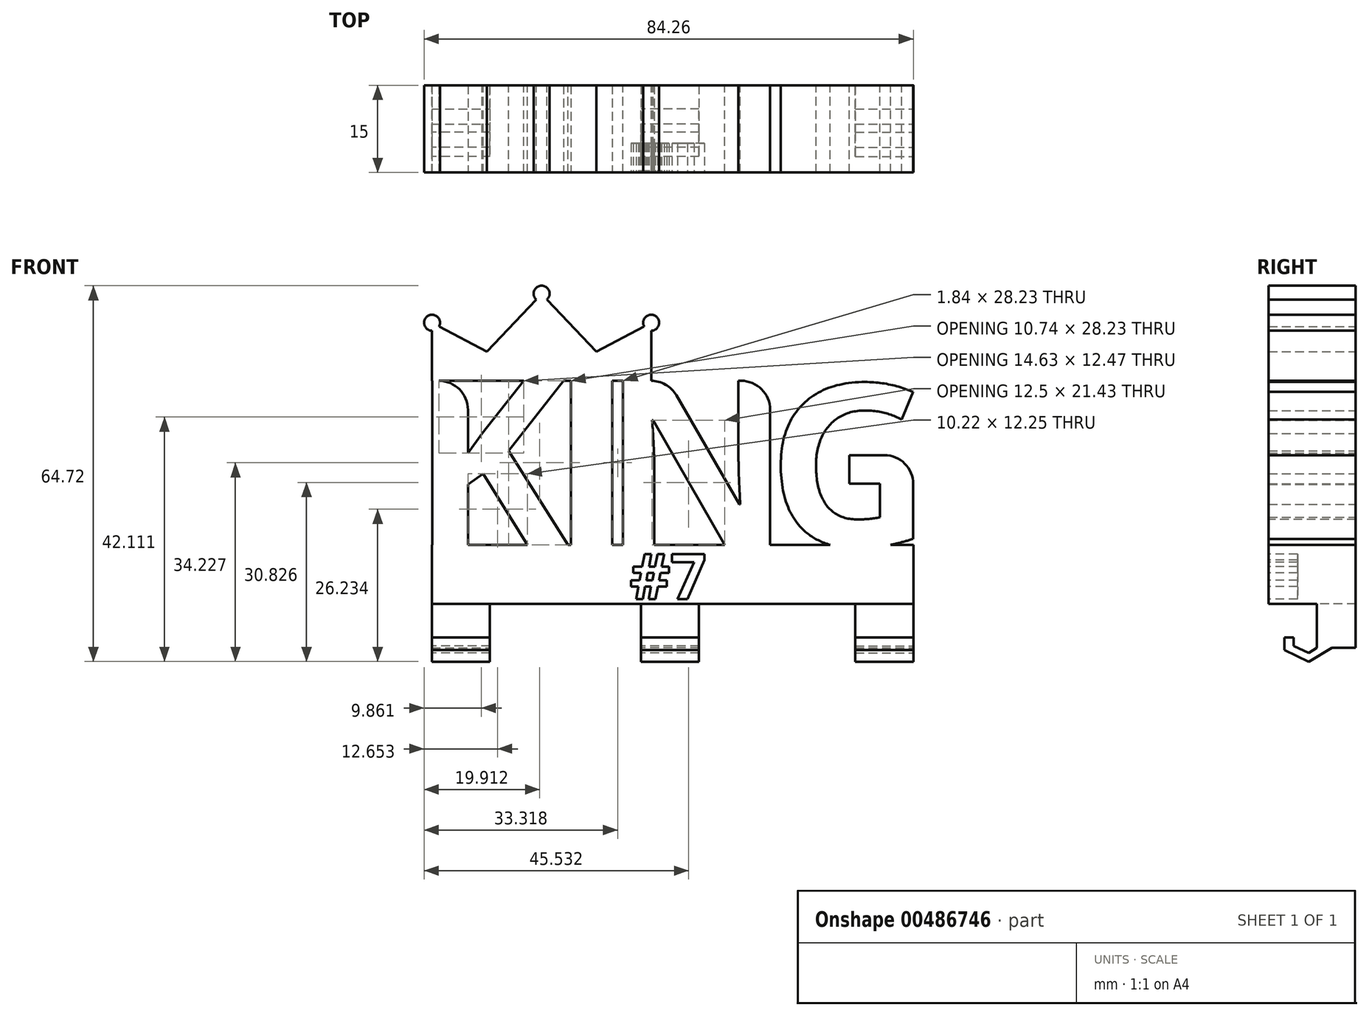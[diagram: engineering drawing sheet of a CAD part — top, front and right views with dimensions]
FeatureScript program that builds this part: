
annotation { "Feature Type Name" : "Feature", "Feature Type Description" : "" }
export const myFeature = defineFeature(function(context is Context, id is Id, definition is map)
    precondition{}
    {
        {
            var Q0;
            Q0=qCreatedBy(makeId("Front.planeOp"),FACE);
            var sketch = newSketch(context, id + "F0", { "sketchPlane" : qUnion([Q0])});
            skLineSegment(sketch, "E0.bottom", {"start": v(-40.14, -20.06) * mm, "end": v(40.04, -20.06) * mm});
            skLineSegment(sketch, "E0.top", {"start": v(-40.14, -9.99) * mm, "end": v(40.04, -9.99) * mm});
            skLineSegment(sketch, "E0.left", {"start": v(-40.14, -20.06) * mm, "end": v(-40.14, -9.99) * mm});
            skLineSegment(sketch, "E0.right", {"start": v(40.04, -20.06) * mm, "end": v(40.04, -9.99) * mm});
            skSolve(sketch);
        }
        {
            var Q0;
            Q0=makeQuery(id+"F0.imprint","IMPRINT",FACE,{"disambiguationData":[TD([[makeQuery(id+"F0.imprint","IMPRINT",EDGE,{"derivedFrom":sQuery(id+"F0.wireOp",EDGE,"E0.bottom")}),1.0]])]});
            extrude(context, id + "F1", {"entities" : qUnion([Q0]), "depth" : 15 * mm});
        }
        {
            var Q0;
            Q0=qCreatedBy(makeId("Front.planeOp"),FACE);
            var sketch = newSketch(context, id + "F2", { "sketchPlane" : qUnion([Q0])});
            skText(sketch, "E1", { "text": "K", "fontName": "OpenSans-Bold.ttf"});
            const initialGuessF2  = {"E1": [-0.0434, -0.00988, 1, 0, 0.02932]};
            skSetInitialGuess(sketch, initialGuessF2);
            skSolve(sketch);
        }
        {
            var Q0;
            Q0 = qSketchRegion(id + "F2", true);
            extrude(context, id + "F3", {"entities" : qUnion([Q0]), "depth" : 15 * mm});
        }
        {
            var Q0;
            Q0=qCreatedBy(makeId("Front.planeOp"),FACE);
            var sketch = newSketch(context, id + "F4", { "sketchPlane" : qUnion([Q0])});
            skLineSegment(sketch, "E2.bottom", {"start": v(-15.84, 19.23) * mm, "end": v(-8.72, 19.23) * mm});
            skLineSegment(sketch, "E2.top", {"start": v(-15.84, -9.97) * mm, "end": v(-8.72, -9.97) * mm});
            skLineSegment(sketch, "E2.left", {"start": v(-15.84, 19.23) * mm, "end": v(-15.84, -9.97) * mm});
            skLineSegment(sketch, "E2.right", {"start": v(-8.72, 19.23) * mm, "end": v(-8.72, -9.97) * mm});
            skSolve(sketch);
        }
        {
            var Q0;
            Q0 = qSketchRegion(id + "F4", true);
            extrude(context, id + "F5", {"entities" : qUnion([Q0]), "depth" : 15 * mm});
        }
        {
            var Q0;
            Q0=qCreatedBy(makeId("Front.planeOp"),FACE);
            var sketch = newSketch(context, id + "F6", { "sketchPlane" : qUnion([Q0])});
            skText(sketch, "E3", { "text": "N", "fontName": "OpenSans-Bold.ttf"});
            const initialGuessF6  = {"E3": [-0.01048, -0.01007, 1, 0, 0.02883]};
            skSetInitialGuess(sketch, initialGuessF6);
            skSolve(sketch);
        }
        {
            var Q0;
            Q0 = qSketchRegion(id + "F6", true);
            extrude(context, id + "F7", {"entities" : qUnion([Q0]), "operationType" : NewBodyOperationType.ADD, "depth" : 15 * mm});
        }
        {
            var Q0;
            Q0=qCreatedBy(makeId("Front.planeOp"),FACE);
            var sketch = newSketch(context, id + "F8", { "sketchPlane" : qUnion([Q0])});
            skText(sketch, "E4", { "text": "G", "fontName": "OpenSans-Bold.ttf"});
            const initialGuessF8  = {"E4": [0.01804, -0.01005, 1, 0, 0.02804]};
            skSetInitialGuess(sketch, initialGuessF8);
            skSolve(sketch);
        }
        {
            var Q0;
            Q0 = qSketchRegion(id + "F8", true);
            extrude(context, id + "F9", {"entities" : qUnion([Q0]), "operationType" : NewBodyOperationType.ADD, "depth" : 15 * mm});
        }
        {
            var Q0;
            Q0=qCreatedBy(makeId("Front.planeOp"),FACE);
            var sketch = newSketch(context, id + "F10", { "sketchPlane" : qUnion([Q0])});
            skLineSegment(sketch, "E5.bottom", {"start": v(-40.2, -19.96) * mm, "end": v(43.48, -19.96) * mm});
            skLineSegment(sketch, "E5.top", {"start": v(-40.2, -10) * mm, "end": v(43.48, -10) * mm});
            skLineSegment(sketch, "E5.left", {"start": v(-40.2, -19.96) * mm, "end": v(-40.2, -10) * mm});
            skLineSegment(sketch, "E5.right", {"start": v(43.48, -19.96) * mm, "end": v(43.48, -10) * mm});
            skSolve(sketch);
        }
        {
            var Q0;
            Q0 = qSketchRegion(id + "F10", true);
            extrude(context, id + "F11", {"entities" : qUnion([Q0]), "operationType" : NewBodyOperationType.ADD, "depth" : 15 * mm});
        }
        {
            var Q0;
            Q0=qCreatedBy(makeId("Front.planeOp"),FACE);
            var sketch = newSketch(context, id + "F12", { "sketchPlane" : qUnion([Q0])});
            skLineSegment(sketch, "E6.bottom", {"start": v(-46.89, 43.54) * mm, "end": v(51.78, 43.54) * mm});
            skLineSegment(sketch, "E6.top", {"start": v(-46.89, 18.35) * mm, "end": v(51.78, 18.35) * mm});
            skLineSegment(sketch, "E6.left", {"start": v(-46.89, 43.54) * mm, "end": v(-46.89, 18.35) * mm});
            skLineSegment(sketch, "E6.right", {"start": v(51.78, 43.54) * mm, "end": v(51.78, 18.35) * mm});
            skSolve(sketch);
        }
        {
            var Q0;
            Q0=makeQuery(id+"F12.imprint","IMPRINT",FACE,{"disambiguationData":[TD([[makeQuery(id+"F12.imprint","IMPRINT",EDGE,{"derivedFrom":sQuery(id+"F12.wireOp",EDGE,"E6.bottom")}),-1.0]])]});
            extrude(context, id + "F13", {"entities" : qUnion([Q0]), "operationType" : NewBodyOperationType.REMOVE, "depth" : 52.6 * mm});
        }
        {
            var Q0;
            Q0=qCreatedBy(makeId("Front.planeOp"),FACE);
            var sketch = newSketch(context, id + "F14", { "sketchPlane" : qUnion([Q0])});
            skLineSegment(sketch, "E7.bottom", {"start": v(-46.08, -4.47) * mm, "end": v(-39.9, -4.47) * mm});
            skLineSegment(sketch, "E7.top", {"start": v(-46.08, -23.6) * mm, "end": v(-39.9, -23.6) * mm});
            skLineSegment(sketch, "E7.left", {"start": v(-46.08, -4.47) * mm, "end": v(-46.08, -23.6) * mm});
            skLineSegment(sketch, "E7.right", {"start": v(-39.9, -4.47) * mm, "end": v(-39.9, -23.6) * mm});
            skSolve(sketch);
        }
        {
            var Q0;
            Q0=makeQuery(id+"F14.imprint","IMPRINT",FACE,{"disambiguationData":[TD([[makeQuery(id+"F14.imprint","IMPRINT",EDGE,{"derivedFrom":sQuery(id+"F14.wireOp",EDGE,"E7.bottom")}),-1.0]])]});
            extrude(context, id + "F15", {"entities" : qUnion([Q0]), "operationType" : NewBodyOperationType.REMOVE, "depth" : 25 * mm});
        }
        {
            var Q0;
            Q0=qCreatedBy(makeId("Front.planeOp"),FACE);
            var sketch = newSketch(context, id + "F16", { "sketchPlane" : qUnion([Q0])});
            skLineSegment(sketch, "E8.bottom", {"start": v(43.14, 5.6) * mm, "end": v(49.6, 5.6) * mm});
            skLineSegment(sketch, "E8.top", {"start": v(43.14, -21.5) * mm, "end": v(49.6, -21.5) * mm});
            skLineSegment(sketch, "E8.left", {"start": v(43.14, 5.6) * mm, "end": v(43.14, -21.5) * mm});
            skLineSegment(sketch, "E8.right", {"start": v(49.6, 5.6) * mm, "end": v(49.6, -21.5) * mm});
            skSolve(sketch);
        }
        {
            var Q0;
            Q0 = qSketchRegion(id + "F16", true);
            extrude(context, id + "F17", {"entities" : qUnion([Q0]), "operationType" : NewBodyOperationType.REMOVE, "depth" : 25 * mm});
        }
        {
            var Q0;
            Q0=qCreatedBy(makeId("Front.planeOp"),FACE);
            var sketch = newSketch(context, id + "F18", { "sketchPlane" : qUnion([Q0])});
            skLineSegment(sketch, "E9.bottom", {"start": v(-39.9, -18.54) * mm, "end": v(43.14, -18.54) * mm});
            skLineSegment(sketch, "E9.top", {"start": v(-39.9, -20.07) * mm, "end": v(43.14, -20.07) * mm});
            skLineSegment(sketch, "E9.left", {"start": v(-39.9, -18.54) * mm, "end": v(-39.9, -20.07) * mm});
            skLineSegment(sketch, "E9.right", {"start": v(43.14, -18.54) * mm, "end": v(43.14, -20.07) * mm});
            skSolve(sketch);
        }
        {
            var Q0;
            Q0 = qSketchRegion(id + "F18", true);
            extrude(context, id + "F19", {"entities" : qUnion([Q0]), "depth" : 15 * mm});
        }
        {
            var Q0;
            Q0=qCreatedBy(makeId("Front.planeOp"),FACE);
            var sketch = newSketch(context, id + "F20", { "sketchPlane" : qUnion([Q0])});
            skLineSegment(sketch, "E10.bottom", {"start": v(-39.9, -10.02) * mm, "end": v(43.14, -10.02) * mm});
            skLineSegment(sketch, "E10.top", {"start": v(-39.9, -9.88) * mm, "end": v(43.14, -9.88) * mm});
            skLineSegment(sketch, "E10.left", {"start": v(-39.9, -10.02) * mm, "end": v(-39.9, -9.88) * mm});
            skLineSegment(sketch, "E10.right", {"start": v(43.14, -10.02) * mm, "end": v(43.14, -9.88) * mm});
            skSolve(sketch);
        }
        {
            var Q0;
            Q0 = qSketchRegion(id + "F20", true);
            extrude(context, id + "F21", {"entities" : qUnion([Q0]), "operationType" : NewBodyOperationType.ADD, "depth" : 15 * mm});
        }
        {
            var Q0;
            Q0=qCreatedBy(makeId("Front.planeOp"),FACE);
            var sketch = newSketch(context, id + "F22", { "sketchPlane" : qUnion([Q0])});
            skLineSegment(sketch, "E11.bottom", {"start": v(-43.65, -8.35) * mm, "end": v(-39.8, -8.35) * mm});
            skLineSegment(sketch, "E11.top", {"start": v(-43.65, -21.4) * mm, "end": v(-39.8, -21.4) * mm});
            skLineSegment(sketch, "E11.left", {"start": v(-43.65, -8.35) * mm, "end": v(-43.65, -21.4) * mm});
            skLineSegment(sketch, "E11.right", {"start": v(-39.8, -8.35) * mm, "end": v(-39.8, -21.4) * mm});
            skSolve(sketch);
        }
        {
            var Q0;
            Q0 = qSketchRegion(id + "F22", true);
            extrude(context, id + "F23", {"entities" : qUnion([Q0]), "operationType" : NewBodyOperationType.REMOVE, "depth" : 25 * mm});
        }
        {
            var Q0;
            {var subQ54=sQuery(id+"F0.wireOp",EDGE,"E0.bottom");Q0=makeQuery(id+"F23.boolean.opBoolean","COPY",FACE,{"disambiguationData":[TD([makeQuery(id+"F1.opExtrude","SWEPT_FACE",FACE,{"disambiguationData":[OSD([subQ54])]})])],"derivedFrom":makeQuery(id+"F23.opExtrude","SWEPT_FACE",FACE,{"disambiguationData":[OSD([sQuery(id+"F22.wireOp",EDGE,"E11.right")])]})});}
            var sketch = newSketch(context, id + "F24", { "sketchPlane" : qUnion([Q0])});
            skLineSegment(sketch, "E12", {"start": v(4.05, -20.06) * mm, "end": v(4.05, -27.64) * mm});
            skLineSegment(sketch, "E13", {"start": v(4.05, -27.64) * mm, "end": v(8.1, -30) * mm});
            skLineSegment(sketch, "E14", {"start": v(8.1, -30) * mm, "end": v(12.3, -27.97) * mm});
            skLineSegment(sketch, "E15", {"start": v(12.3, -27.97) * mm, "end": v(12.3, -25.82) * mm});
            skLineSegment(sketch, "E16", {"start": v(12.3, -25.82) * mm, "end": v(10.66, -25.82) * mm});
            skLineSegment(sketch, "E17", {"start": v(10.66, -25.82) * mm, "end": v(10.66, -27.31) * mm});
            skLineSegment(sketch, "E18", {"start": v(10.66, -27.31) * mm, "end": v(8.1, -28.47) * mm});
            skLineSegment(sketch, "E19", {"start": v(8.1, -28.47) * mm, "end": v(6.67, -27.64) * mm});
            skLineSegment(sketch, "E20", {"start": v(6.67, -27.64) * mm, "end": v(6.67, -20.06) * mm});
            skLineSegment(sketch, "E21", {"start": v(6.67, -20.06) * mm, "end": v(4.05, -20.06) * mm});
            skSolve(sketch);
        }
        {
            var Q0;
            Q0=makeQuery(id+"F24.imprint","IMPRINT",FACE,{"disambiguationData":[TD([[makeQuery(id+"F24.imprint","IMPRINT",EDGE,{"derivedFrom":sQuery(id+"F24.wireOp",EDGE,"E12")}),1.0]])]});
            extrude(context, id + "F25", {"entities" : qUnion([Q0]), "operationType" : NewBodyOperationType.ADD, "oppositeDirection" : true, "depth" : 10 * mm});
        }
        {
            var Q0;
            Q0=makeQuery(id+"F17.boolean.opBoolean","COPY",FACE,{"derivedFrom":makeQuery(id+"F17.opExtrude","SWEPT_FACE",FACE,{"disambiguationData":[OSD([sQuery(id+"F16.wireOp",EDGE,"E8.left")])]})});
            var sketch = newSketch(context, id + "F26", { "sketchPlane" : qUnion([Q0])});
            skLineSegment(sketch, "E22.0.0", {"start": v(-4.05, -27.64) * mm, "end": v(-4.05, -20.07) * mm});
            skLineSegment(sketch, "E22.0.1", {"start": v(-4.05, -20.07) * mm, "end": v(-6.67, -20.07) * mm});
            skLineSegment(sketch, "E22.0.2", {"start": v(-6.67, -20.07) * mm, "end": v(-6.67, -27.64) * mm});
            skLineSegment(sketch, "E22.0.3", {"start": v(-6.67, -27.64) * mm, "end": v(-8.1, -28.47) * mm});
            skLineSegment(sketch, "E22.0.4", {"start": v(-8.1, -28.47) * mm, "end": v(-10.66, -27.31) * mm});
            skLineSegment(sketch, "E22.0.5", {"start": v(-10.66, -27.31) * mm, "end": v(-10.66, -25.82) * mm});
            skLineSegment(sketch, "E22.0.6", {"start": v(-10.66, -25.82) * mm, "end": v(-12.3, -25.82) * mm});
            skLineSegment(sketch, "E22.0.7", {"start": v(-12.3, -25.82) * mm, "end": v(-12.3, -27.97) * mm});
            skLineSegment(sketch, "E22.0.8", {"start": v(-12.3, -27.97) * mm, "end": v(-8.1, -30) * mm});
            skLineSegment(sketch, "E22.0.9", {"start": v(-8.1, -30) * mm, "end": v(-4.05, -27.64) * mm});
            skSolve(sketch);
        }
        {
            var Q0;
            Q0=makeQuery(id+"F26.imprint","IMPRINT",FACE,{"disambiguationData":[TD([[makeQuery(id+"F26.imprint","IMPRINT",EDGE,{"derivedFrom":sQuery(id+"F26.wireOp",EDGE,"E22.0.0")}),1.0]])]});
            extrude(context, id + "F27", {"entities" : qUnion([Q0]), "operationType" : NewBodyOperationType.ADD, "oppositeDirection" : true, "depth" : 10 * mm});
        }
        {
            var Q0;
            Q0=makeQuery(id+"F25.opExtrude","CAP_FACE",FACE,{"disambiguationData":[OSD([sQuery(id+"F24.wireOp",EDGE,"E12"),sQuery(id+"F24.wireOp",EDGE,"E13"),sQuery(id+"F24.wireOp",EDGE,"E14"),sQuery(id+"F24.wireOp",EDGE,"E15"),sQuery(id+"F24.wireOp",EDGE,"E16"),sQuery(id+"F24.wireOp",EDGE,"E17"),sQuery(id+"F24.wireOp",EDGE,"E18"),sQuery(id+"F24.wireOp",EDGE,"E19"),sQuery(id+"F24.wireOp",EDGE,"E20"),sQuery(id+"F24.wireOp",EDGE,"E21")])],"isStart":false});
            cPlane(context, id + "F28", {"entities" : qUnion([Q0]), "cplaneType" : CPlaneType.OFFSET, "offset" : 26 * mm, "width" : 150 * mm, "height" : 150 * mm});
        }
        {
            var Q0;
            Q0=qCreatedBy(id+"F28.planeOp",FACE);
            var sketch = newSketch(context, id + "F29", { "sketchPlane" : qUnion([Q0])});
            skLineSegment(sketch, "E23.0.0", {"start": v(-4.05, -27.64) * mm, "end": v(-4.05, -20.07) * mm});
            skLineSegment(sketch, "E23.0.1", {"start": v(-4.05, -20.07) * mm, "end": v(-6.67, -20.07) * mm});
            skLineSegment(sketch, "E23.0.2", {"start": v(-6.67, -20.07) * mm, "end": v(-6.67, -27.64) * mm});
            skLineSegment(sketch, "E23.0.3", {"start": v(-6.67, -27.64) * mm, "end": v(-8.1, -28.47) * mm});
            skLineSegment(sketch, "E23.0.4", {"start": v(-8.1, -28.47) * mm, "end": v(-10.66, -27.31) * mm});
            skLineSegment(sketch, "E23.0.5", {"start": v(-10.66, -27.31) * mm, "end": v(-10.66, -25.82) * mm});
            skLineSegment(sketch, "E23.0.6", {"start": v(-10.66, -25.82) * mm, "end": v(-12.3, -25.82) * mm});
            skLineSegment(sketch, "E23.0.7", {"start": v(-12.3, -25.82) * mm, "end": v(-12.3, -27.97) * mm});
            skLineSegment(sketch, "E23.0.8", {"start": v(-12.3, -27.97) * mm, "end": v(-8.1, -30) * mm});
            skLineSegment(sketch, "E23.0.9", {"start": v(-8.1, -30) * mm, "end": v(-4.05, -27.64) * mm});
            skSolve(sketch);
        }
        {
            var Q0;
            Q0=makeQuery(id+"F29.imprint","IMPRINT",FACE,{"disambiguationData":[TD([[makeQuery(id+"F29.imprint","IMPRINT",EDGE,{"derivedFrom":sQuery(id+"F29.wireOp",EDGE,"E23.0.0")}),1.0]])]});
            extrude(context, id + "F30", {"entities" : qUnion([Q0]), "operationType" : NewBodyOperationType.ADD, "depth" : 10 * mm});
        }
        {
            var Q0;
            {var subQ0=sQuery(id+"F18.wireOp",EDGE,"E9.bottom");var subQ4=makeQuery(id+"F23.opExtrude","SWEPT_FACE",FACE,{"disambiguationData":[OSD([sQuery(id+"F22.wireOp",EDGE,"E11.right")])]});var subQ59=sQuery(id+"F0.wireOp",EDGE,"E0.bottom");Q0=makeQuery(id+"F25.boolean.opBoolean","MERGE",FACE,{"derivedFrom":[makeQuery(id+"F23.boolean.opBoolean","COPY",FACE,{"disambiguationData":[TD([makeQuery(id+"F1.opExtrude","SWEPT_FACE",FACE,{"disambiguationData":[OSD([subQ59])]})])],"derivedFrom":subQ4}),makeQuery(id+"F23.boolean.opBoolean","COPY",FACE,{"disambiguationData":[TD([makeQuery(id+"F19.opExtrude","SWEPT_FACE",FACE,{"disambiguationData":[OSD([subQ0])]})])],"derivedFrom":subQ4}),makeQuery(id+"F25.opExtrude","CAP_FACE",FACE,{"disambiguationData":[OSD([sQuery(id+"F24.wireOp",EDGE,"E12"),sQuery(id+"F24.wireOp",EDGE,"E13"),sQuery(id+"F24.wireOp",EDGE,"E14"),sQuery(id+"F24.wireOp",EDGE,"E15"),sQuery(id+"F24.wireOp",EDGE,"E16"),sQuery(id+"F24.wireOp",EDGE,"E17"),sQuery(id+"F24.wireOp",EDGE,"E18"),sQuery(id+"F24.wireOp",EDGE,"E19"),sQuery(id+"F24.wireOp",EDGE,"E20"),sQuery(id+"F24.wireOp",EDGE,"E21")])],"isStart":true})]});}
            var sketch = newSketch(context, id + "F31", { "sketchPlane" : qUnion([Q0])});
            skLineSegment(sketch, "E24.bottom", {"start": v(0, -20.07) * mm, "end": v(4.05, -20.07) * mm});
            skLineSegment(sketch, "E24.top", {"start": v(0, -27.64) * mm, "end": v(4.05, -27.64) * mm});
            skLineSegment(sketch, "E24.left", {"start": v(0, -20.07) * mm, "end": v(0, -27.64) * mm});
            skLineSegment(sketch, "E24.right", {"start": v(4.05, -20.07) * mm, "end": v(4.05, -27.64) * mm});
            skSolve(sketch);
        }
        {
            var Q0;
            Q0=makeQuery(id+"F31.imprint","IMPRINT",FACE,{"disambiguationData":[TD([[makeQuery(id+"F31.imprint","IMPRINT",EDGE,{"derivedFrom":sQuery(id+"F31.wireOp",EDGE,"E24.bottom")}),1.0]])]});
            extrude(context, id + "F32", {"entities" : qUnion([Q0]), "oppositeDirection" : true, "depth" : 10 * mm});
        }
        {
            var Q0;
            Q0=makeQuery(id+"F30.opExtrude","SWEPT_FACE",FACE,{"disambiguationData":[OSD([sQuery(id+"F29.wireOp",EDGE,"E23.0.0")])]});
            var sketch = newSketch(context, id + "F33", { "sketchPlane" : qUnion([Q0])});
            skLineSegment(sketch, "E25.bottom", {"start": v(-6.2, -27.64) * mm, "end": v(3.8, -27.64) * mm});
            skLineSegment(sketch, "E25.top", {"start": v(-6.2, -20.07) * mm, "end": v(3.8, -20.07) * mm});
            skLineSegment(sketch, "E25.left", {"start": v(-6.2, -27.64) * mm, "end": v(-6.2, -20.07) * mm});
            skLineSegment(sketch, "E25.right", {"start": v(3.8, -27.64) * mm, "end": v(3.8, -20.07) * mm});
            skSolve(sketch);
        }
        {
            var Q0;
            Q0 = qSketchRegion(id + "F33", true);
            extrude(context, id + "F34", {"entities" : qUnion([Q0]), "operationType" : NewBodyOperationType.ADD, "depth" : 4.05 * mm});
        }
        {
            var Q0;
            Q0=makeQuery(id+"F27.opExtrude","CAP_FACE",FACE,{"disambiguationData":[OSD([sQuery(id+"F26.wireOp",EDGE,"E22.0.0"),sQuery(id+"F26.wireOp",EDGE,"E22.0.1"),sQuery(id+"F26.wireOp",EDGE,"E22.0.3"),sQuery(id+"F26.wireOp",EDGE,"E22.0.4"),sQuery(id+"F26.wireOp",EDGE,"E22.0.5"),sQuery(id+"F26.wireOp",EDGE,"E22.0.6"),sQuery(id+"F26.wireOp",EDGE,"E22.0.7"),sQuery(id+"F26.wireOp",EDGE,"E22.0.8"),sQuery(id+"F26.wireOp",EDGE,"E22.0.9"),sQuery(id+"F26.wireOp",EDGE,"E22.0.2")])],"isStart":true});
            var sketch = newSketch(context, id + "F35", { "sketchPlane" : qUnion([Q0])});
            skLineSegment(sketch, "E26.bottom", {"start": v(-4.05, -20.07) * mm, "end": v(0, -20.07) * mm});
            skLineSegment(sketch, "E26.top", {"start": v(-4.05, -27.64) * mm, "end": v(0, -27.64) * mm});
            skLineSegment(sketch, "E26.left", {"start": v(-4.05, -20.07) * mm, "end": v(-4.05, -27.64) * mm});
            skLineSegment(sketch, "E26.right", {"start": v(0, -20.07) * mm, "end": v(0, -27.64) * mm});
            skSolve(sketch);
        }
        {
            var Q0;
            Q0 = qSketchRegion(id + "F35", true);
            extrude(context, id + "F36", {"entities" : qUnion([Q0]), "operationType" : NewBodyOperationType.ADD, "oppositeDirection" : true, "depth" : 10 * mm});
        }
        {
            var Q0;
            {var subQ0=sQuery(id+"F18.wireOp",EDGE,"E9.bottom");var subQ4=makeQuery(id+"F23.opExtrude","SWEPT_FACE",FACE,{"disambiguationData":[OSD([sQuery(id+"F22.wireOp",EDGE,"E11.right")])]});var subQ59=sQuery(id+"F0.wireOp",EDGE,"E0.bottom");Q0=makeQuery(id+"F25.boolean.opBoolean","MERGE",FACE,{"derivedFrom":[makeQuery(id+"F23.boolean.opBoolean","COPY",FACE,{"disambiguationData":[TD([makeQuery(id+"F1.opExtrude","SWEPT_FACE",FACE,{"disambiguationData":[OSD([subQ59])]})])],"derivedFrom":subQ4}),makeQuery(id+"F23.boolean.opBoolean","COPY",FACE,{"disambiguationData":[TD([makeQuery(id+"F19.opExtrude","SWEPT_FACE",FACE,{"disambiguationData":[OSD([subQ0])]})])],"derivedFrom":subQ4}),makeQuery(id+"F25.opExtrude","CAP_FACE",FACE,{"disambiguationData":[OSD([sQuery(id+"F24.wireOp",EDGE,"E12"),sQuery(id+"F24.wireOp",EDGE,"E13"),sQuery(id+"F24.wireOp",EDGE,"E14"),sQuery(id+"F24.wireOp",EDGE,"E15"),sQuery(id+"F24.wireOp",EDGE,"E16"),sQuery(id+"F24.wireOp",EDGE,"E17"),sQuery(id+"F24.wireOp",EDGE,"E18"),sQuery(id+"F24.wireOp",EDGE,"E19"),sQuery(id+"F24.wireOp",EDGE,"E20"),sQuery(id+"F24.wireOp",EDGE,"E21")])],"isStart":true})]});}
            var sketch = newSketch(context, id + "F37", { "sketchPlane" : qUnion([Q0])});
            skLineSegment(sketch, "E27.bottom", {"start": v(4.8, -17.53) * mm, "end": v(0, -17.53) * mm});
            skLineSegment(sketch, "E27.top", {"start": v(4.8, -27.64) * mm, "end": v(0, -27.64) * mm});
            skLineSegment(sketch, "E27.left", {"start": v(4.8, -17.53) * mm, "end": v(4.8, -27.64) * mm});
            skLineSegment(sketch, "E27.right", {"start": v(0, -17.53) * mm, "end": v(0, -27.64) * mm});
            skSolve(sketch);
        }
        {
            var Q0;
            Q0 = qSketchRegion(id + "F37", true);
            extrude(context, id + "F38", {"entities" : qUnion([Q0]), "operationType" : NewBodyOperationType.ADD, "oppositeDirection" : true, "depth" : 10 * mm});
        }
        {
            var Q0;
            Q0=makeQuery(id+"F13.boolean.opBoolean","INTERSECT",EDGE,{"derivedFrom":[makeQuery(id+"F7.opExtrude","SWEPT_FACE",FACE,{"disambiguationData":[OSD([sQuery(id+"F6.wireOp",EDGE,"E3.sketch_text.stroke-8")])]}),makeQuery(id+"F13.opExtrude","SWEPT_FACE",FACE,{"disambiguationData":[OSD([sQuery(id+"F12.wireOp",EDGE,"E6.top")])]})]});
            fillet(context, id + "F39", {"entities" : qUnion([Q0]), "radius" : 5 * mm, "tangentPropagation" : true, "allowEdgeOverflow" : false});
        }
        {
            var Q0;
            Q0=makeQuery(id+"F9.opExtrude","SWEPT_EDGE",EDGE,{"disambiguationData":[OSD([sQuery(id+"F8.wireOp",EDGE,"E4.sketch_text.stroke-0"),sQuery(id+"F8.wireOp",EDGE,"E4.sketch_text.stroke-1")])]});
            fillet(context, id + "F40", {"entities" : qUnion([Q0]), "radius" : 5 * mm, "tangentPropagation" : true, "allowEdgeOverflow" : false});
        }
        {
            var Q0;
            Q0=makeQuery(id+"F13.boolean.opBoolean","INTERSECT",EDGE,{"derivedFrom":[makeQuery(id+"F3.opExtrude","SWEPT_FACE",FACE,{"disambiguationData":[OSD([sQuery(id+"F2.wireOp",EDGE,"E1.sketch_text.stroke-7")])]}),makeQuery(id+"F13.opExtrude","SWEPT_FACE",FACE,{"disambiguationData":[OSD([sQuery(id+"F12.wireOp",EDGE,"E6.top")])]})]});
            var Q1;
            Q1=makeQuery(id+"F13.boolean.opBoolean","INTERSECT",EDGE,{"derivedFrom":[makeQuery(id+"F7.opExtrude","SWEPT_FACE",FACE,{"disambiguationData":[OSD([sQuery(id+"F6.wireOp",EDGE,"E3.sketch_text.stroke-13")])]}),makeQuery(id+"F13.opExtrude","SWEPT_FACE",FACE,{"disambiguationData":[OSD([sQuery(id+"F12.wireOp",EDGE,"E6.top")])]})]});
            fillet(context, id + "F41", {"entities" : qUnion([Q0, Q1]), "radius" : 5 * mm, "tangentPropagation" : true, "allowEdgeOverflow" : false});
        }
        {
            var Q0;
            Q0=qCreatedBy(makeId("Front.planeOp"),FACE);
            var sketch = newSketch(context, id + "F42", { "sketchPlane" : qUnion([Q0])});
            skLineSegment(sketch, "E28.0.0", {"start": v(18.47, -9.88) * mm, "end": v(18.47, 13.35) * mm});
            skArc(sketch, "E28.0.1", {"start": v(18.47, 13.35) * mm, "mid": v(17.01, 16.9) * mm, "end": v(13.47, 18.35) * mm});
            skLineSegment(sketch, "E28.0.2", {"start": v(13.47, 18.35) * mm, "end": v(13.02, 18.35) * mm});
            skLineSegment(sketch, "E28.0.3", {"start": v(13.02, 18.35) * mm, "end": v(13.02, 4.99) * mm});
            skFitSpline(sketch, "E28.0.4", {"points": [v(13.02, 4.99) * mm, v(13.02, 2.69) * mm, v(13.31, -2.89) * mm]});
            skLineSegment(sketch, "E28.0.5", {"start": v(13.31, -2.89) * mm, "end": v(13.17, -2.89) * mm});
            skLineSegment(sketch, "E28.0.6", {"start": v(13.17, -2.89) * mm, "end": v(2.3, 15.86) * mm});
            skArc(sketch, "E28.0.7", {"start": v(2.3, 15.86) * mm, "mid": v(0.47, 17.69) * mm, "end": v(-2.02, 18.35) * mm});
            skLineSegment(sketch, "E28.0.8", {"start": v(-2.02, 18.35) * mm, "end": v(-6.89, 18.35) * mm});
            skLineSegment(sketch, "E28.0.9", {"start": v(-6.89, 18.35) * mm, "end": v(-6.89, -9.88) * mm});
            skLineSegment(sketch, "E28.0.10", {"start": v(-6.89, -9.88) * mm, "end": v(-8.72, -9.88) * mm});
            skLineSegment(sketch, "E28.0.11", {"start": v(-8.72, -9.88) * mm, "end": v(-8.72, 18.35) * mm});
            skLineSegment(sketch, "E28.0.12", {"start": v(-8.72, 18.35) * mm, "end": v(-15.84, 18.35) * mm});
            skLineSegment(sketch, "E28.0.13", {"start": v(-15.84, 18.35) * mm, "end": v(-15.84, -9.88) * mm});
            skFitSpline(sketch, "E28.0.14", {"points": [v(-15.84, -9.88) * mm, v(-16.01, -9.88) * mm, v(-16.19, -9.88) * mm, v(-16.36, -9.88) * mm]});
            skLineSegment(sketch, "E28.0.15", {"start": v(-16.36, -9.88) * mm, "end": v(-26.58, 6.32) * mm});
            skLineSegment(sketch, "E28.0.16", {"start": v(-26.58, 6.32) * mm, "end": v(-17.1, 18.35) * mm});
            skLineSegment(sketch, "E28.0.17", {"start": v(-17.1, 18.35) * mm, "end": v(-23.95, 18.35) * mm});
            skLineSegment(sketch, "E28.0.18", {"start": v(-23.95, 18.35) * mm, "end": v(-31.16, 9.3) * mm});
            skLineSegment(sketch, "E28.0.19", {"start": v(-31.16, 9.3) * mm, "end": v(-33.58, 5.88) * mm});
            skLineSegment(sketch, "E28.0.20", {"start": v(-33.58, 5.88) * mm, "end": v(-33.58, 13.35) * mm});
            skArc(sketch, "E28.0.21", {"start": v(-33.58, 13.35) * mm, "mid": v(-35.05, 16.9) * mm, "end": v(-38.58, 18.35) * mm});
            skLineSegment(sketch, "E28.0.22", {"start": v(-38.58, 18.35) * mm, "end": v(-39.75, 18.35) * mm});
            skLineSegment(sketch, "E28.0.23", {"start": v(-39.75, 18.35) * mm, "end": v(-39.75, -9.88) * mm});
            skFitSpline(sketch, "E28.0.24", {"points": [v(-39.75, -9.88) * mm, v(-39.76, -9.88) * mm, v(-39.78, -9.88) * mm, v(-39.8, -9.88) * mm]});
            skLineSegment(sketch, "E28.0.25", {"start": v(-39.8, -9.88) * mm, "end": v(-39.8, -20.07) * mm});
            skLineSegment(sketch, "E28.0.26", {"start": v(-39.8, -20.07) * mm, "end": v(43.14, -20.07) * mm});
            skFitSpline(sketch, "E28.0.27", {"points": [v(43.14, -20.07) * mm, v(43.14, -20.04) * mm, v(43.14, -20) * mm, v(43.14, -19.96) * mm]});
            skLineSegment(sketch, "E28.0.28", {"start": v(43.14, -19.96) * mm, "end": v(43.14, -18.54) * mm});
            skFitSpline(sketch, "E28.0.29", {"points": [v(43.14, -18.54) * mm, v(43.14, -15.7) * mm, v(43.14, -12.86) * mm, v(43.14, -10.02) * mm]});
            skFitSpline(sketch, "E28.0.30", {"points": [v(43.14, -10) * mm, v(43.14, -9.96) * mm, v(43.14, -9.92) * mm, v(43.14, -9.88) * mm]});
            skLineSegment(sketch, "E28.0.31", {"start": v(43.14, -9.88) * mm, "end": v(39.24, -9.88) * mm});
            skFitSpline(sketch, "E28.0.32", {"points": [v(38.07, -10.08) * mm, v(40.44, -9.73) * mm, v(43.13, -8.85) * mm]});
            skLineSegment(sketch, "E28.0.33", {"start": v(43.13, -8.85) * mm, "end": v(43.13, 0.56) * mm});
            skArc(sketch, "E28.0.34", {"start": v(43.13, 0.56) * mm, "mid": v(41.66, 4.1) * mm, "end": v(38.13, 5.56) * mm});
            skLineSegment(sketch, "E28.0.35", {"start": v(38.13, 5.56) * mm, "end": v(32.1, 5.56) * mm});
            skLineSegment(sketch, "E28.0.36", {"start": v(32.1, 5.56) * mm, "end": v(32.1, 0.65) * mm});
            skLineSegment(sketch, "E28.0.37", {"start": v(32.1, 0.65) * mm, "end": v(37.36, 0.65) * mm});
            skLineSegment(sketch, "E28.0.38", {"start": v(37.36, 0.65) * mm, "end": v(37.36, -5.15) * mm});
            skFitSpline(sketch, "E28.0.39", {"points": [v(37.36, -5.15) * mm, v(35.46, -5.52) * mm, v(33.61, -5.52) * mm]});
            skFitSpline(sketch, "E28.0.40", {"points": [v(33.61, -5.52) * mm, v(30.08, -5.52) * mm, v(28.23, -3.14) * mm]});
            skFitSpline(sketch, "E28.0.41", {"points": [v(28.23, -3.14) * mm, v(26.37, -0.75) * mm, v(26.37, 3.77) * mm]});
            skFitSpline(sketch, "E28.0.42", {"points": [v(26.37, 3.77) * mm, v(26.37, 8.1) * mm, v(28.67, 10.68) * mm]});
            skFitSpline(sketch, "E28.0.43", {"points": [v(28.67, 10.68) * mm, v(30.97, 13.24) * mm, v(34.8, 13.24) * mm]});
            skFitSpline(sketch, "E28.0.44", {"points": [v(34.8, 13.24) * mm, v(38.09, 13.24) * mm, v(41.13, 11.72) * mm]});
            skLineSegment(sketch, "E28.0.45", {"start": v(41.13, 11.72) * mm, "end": v(43.09, 16.44) * mm});
            skFitSpline(sketch, "E28.0.46", {"points": [v(43.09, 16.44) * mm, v(39.12, 18.15) * mm, v(34.83, 18.15) * mm]});
            skFitSpline(sketch, "E28.0.47", {"points": [v(34.83, 18.15) * mm, v(28, 18.15) * mm, v(24.16, 14.38) * mm]});
            skFitSpline(sketch, "E28.0.48", {"points": [v(24.16, 14.38) * mm, v(20.3, 10.62) * mm, v(20.3, 3.9) * mm]});
            skFitSpline(sketch, "E28.0.49", {"points": [v(20.3, 3.9) * mm, v(20.3, -3.04) * mm, v(23.63, -6.74) * mm]});
            skFitSpline(sketch, "E28.0.50", {"points": [v(23.63, -6.74) * mm, v(26.94, -10.43) * mm, v(33.24, -10.43) * mm]});
            skLineSegment(sketch, "E28.0.51", {"start": v(28.8, -9.88) * mm, "end": v(18.47, -9.88) * mm});
            skLineSegment(sketch, "E29", {"start": v(-39.75, 18.35) * mm, "end": v(-2.02, 18.35) * mm});
            skLineSegment(sketch, "E30", {"start": v(-39.75, 18.35) * mm, "end": v(-39.75, 28.35) * mm});
            skPoint(sketch, "E31.endSnap0", {"position": v(-39.75, 23.35) * mm});
            skLineSegment(sketch, "E32", {"start": v(-2.02, 18.35) * mm, "end": v(-2.02, 28.35) * mm});
            skLineSegment(sketch, "E33", {"start": v(-39.75, 28.35) * mm, "end": v(-30.32, 23.35) * mm});
            skLineSegment(sketch, "E34", {"start": v(-30.32, 23.35) * mm, "end": v(-20.88, 33.35) * mm});
            skLineSegment(sketch, "E35", {"start": v(-20.88, 33.35) * mm, "end": v(-11.45, 23.35) * mm});
            skLineSegment(sketch, "E36", {"start": v(-2.02, 28.35) * mm, "end": v(-11.45, 23.35) * mm});
            skSolve(sketch);
        }
        {
            var Q0;
            {var subQ1=sQuery(id+"F42.wireOp",EDGE,"E30");Q0=makeQuery(id+"F42.imprint","IMPRINT",FACE,{"disambiguationData":[TD([[makeQuery(id+"F42.imprint","IMPRINT",EDGE,{"derivedFrom":subQ1}),-1.0]])]});}
            extrude(context, id + "F43", {"entities" : qUnion([Q0]), "operationType" : NewBodyOperationType.ADD, "depth" : 15 * mm});
        }
        {
            var Q0;
            Q0=qCreatedBy(makeId("Front.planeOp"),FACE);
            var sketch = newSketch(context, id + "F44", { "sketchPlane" : qUnion([Q0])});
            skLineSegment(sketch, "E37.0.0", {"start": v(18.47, -9.88) * mm, "end": v(18.47, 13.35) * mm});
            skArc(sketch, "E37.0.1", {"start": v(18.47, 13.35) * mm, "mid": v(17.01, 16.9) * mm, "end": v(13.47, 18.35) * mm});
            skLineSegment(sketch, "E37.0.2", {"start": v(13.47, 18.35) * mm, "end": v(13.02, 18.35) * mm});
            skLineSegment(sketch, "E37.0.3", {"start": v(13.02, 18.35) * mm, "end": v(13.02, 4.99) * mm});
            skFitSpline(sketch, "E37.0.4", {"points": [v(13.02, 4.99) * mm, v(13.02, 2.69) * mm, v(13.31, -2.89) * mm]});
            skLineSegment(sketch, "E37.0.5", {"start": v(13.31, -2.89) * mm, "end": v(13.17, -2.89) * mm});
            skLineSegment(sketch, "E37.0.6", {"start": v(13.17, -2.89) * mm, "end": v(2.3, 15.86) * mm});
            skArc(sketch, "E37.0.7", {"start": v(2.3, 15.86) * mm, "mid": v(0.47, 17.69) * mm, "end": v(-2.02, 18.35) * mm});
            skLineSegment(sketch, "E37.0.8", {"start": v(-2.02, 18.35) * mm, "end": v(-2.02, 28.35) * mm});
            skLineSegment(sketch, "E37.0.9", {"start": v(-2.02, 28.35) * mm, "end": v(-11.45, 23.35) * mm});
            skLineSegment(sketch, "E37.0.10", {"start": v(-11.45, 23.35) * mm, "end": v(-20.88, 33.35) * mm});
            skLineSegment(sketch, "E37.0.11", {"start": v(-20.88, 33.35) * mm, "end": v(-30.32, 23.35) * mm});
            skLineSegment(sketch, "E37.0.12", {"start": v(-30.32, 23.35) * mm, "end": v(-39.75, 28.35) * mm});
            skLineSegment(sketch, "E37.0.13", {"start": v(-39.75, 28.35) * mm, "end": v(-39.75, -9.88) * mm});
            skFitSpline(sketch, "E37.0.14", {"points": [v(-39.75, -9.88) * mm, v(-39.76, -9.88) * mm, v(-39.78, -9.88) * mm, v(-39.8, -9.88) * mm]});
            skLineSegment(sketch, "E37.0.15", {"start": v(-39.8, -9.88) * mm, "end": v(-39.8, -20.07) * mm});
            skLineSegment(sketch, "E37.0.16", {"start": v(-39.8, -20.07) * mm, "end": v(43.14, -20.07) * mm});
            skFitSpline(sketch, "E37.0.17", {"points": [v(43.14, -20.07) * mm, v(43.14, -20.04) * mm, v(43.14, -20) * mm, v(43.14, -19.96) * mm]});
            skLineSegment(sketch, "E37.0.18", {"start": v(43.14, -19.96) * mm, "end": v(43.14, -18.54) * mm});
            skFitSpline(sketch, "E37.0.19", {"points": [v(43.14, -18.54) * mm, v(43.14, -15.7) * mm, v(43.14, -12.86) * mm, v(43.14, -10.02) * mm]});
            skFitSpline(sketch, "E37.0.20", {"points": [v(43.14, -10) * mm, v(43.14, -9.96) * mm, v(43.14, -9.92) * mm, v(43.14, -9.88) * mm]});
            skLineSegment(sketch, "E37.0.21", {"start": v(43.14, -9.88) * mm, "end": v(39.24, -9.88) * mm});
            skFitSpline(sketch, "E37.0.22", {"points": [v(38.07, -10.08) * mm, v(40.44, -9.73) * mm, v(43.13, -8.85) * mm]});
            skLineSegment(sketch, "E37.0.23", {"start": v(43.13, -8.85) * mm, "end": v(43.13, 0.56) * mm});
            skArc(sketch, "E37.0.24", {"start": v(43.13, 0.56) * mm, "mid": v(41.66, 4.1) * mm, "end": v(38.13, 5.56) * mm});
            skLineSegment(sketch, "E37.0.25", {"start": v(38.13, 5.56) * mm, "end": v(32.1, 5.56) * mm});
            skLineSegment(sketch, "E37.0.26", {"start": v(32.1, 5.56) * mm, "end": v(32.1, 0.65) * mm});
            skLineSegment(sketch, "E37.0.27", {"start": v(32.1, 0.65) * mm, "end": v(37.36, 0.65) * mm});
            skLineSegment(sketch, "E37.0.28", {"start": v(37.36, 0.65) * mm, "end": v(37.36, -5.15) * mm});
            skFitSpline(sketch, "E37.0.29", {"points": [v(37.36, -5.15) * mm, v(35.46, -5.52) * mm, v(33.61, -5.52) * mm]});
            skFitSpline(sketch, "E37.0.30", {"points": [v(33.61, -5.52) * mm, v(30.08, -5.52) * mm, v(28.23, -3.14) * mm]});
            skFitSpline(sketch, "E37.0.31", {"points": [v(28.23, -3.14) * mm, v(26.37, -0.75) * mm, v(26.37, 3.77) * mm]});
            skFitSpline(sketch, "E37.0.32", {"points": [v(26.37, 3.77) * mm, v(26.37, 8.1) * mm, v(28.67, 10.68) * mm]});
            skFitSpline(sketch, "E37.0.33", {"points": [v(28.67, 10.68) * mm, v(30.97, 13.24) * mm, v(34.8, 13.24) * mm]});
            skFitSpline(sketch, "E37.0.34", {"points": [v(34.8, 13.24) * mm, v(38.09, 13.24) * mm, v(41.13, 11.72) * mm]});
            skLineSegment(sketch, "E37.0.35", {"start": v(41.13, 11.72) * mm, "end": v(43.09, 16.44) * mm});
            skFitSpline(sketch, "E37.0.36", {"points": [v(43.09, 16.44) * mm, v(39.12, 18.15) * mm, v(34.83, 18.15) * mm]});
            skFitSpline(sketch, "E37.0.37", {"points": [v(34.83, 18.15) * mm, v(28, 18.15) * mm, v(24.16, 14.38) * mm]});
            skFitSpline(sketch, "E37.0.38", {"points": [v(24.16, 14.38) * mm, v(20.3, 10.62) * mm, v(20.3, 3.9) * mm]});
            skFitSpline(sketch, "E37.0.39", {"points": [v(20.3, 3.9) * mm, v(20.3, -3.04) * mm, v(23.63, -6.74) * mm]});
            skFitSpline(sketch, "E37.0.40", {"points": [v(23.63, -6.74) * mm, v(26.94, -10.43) * mm, v(33.24, -10.43) * mm]});
            skLineSegment(sketch, "E37.0.41", {"start": v(28.8, -9.88) * mm, "end": v(18.47, -9.88) * mm});
            skCircle(sketch, "E38", {"center": v(-20.88, 33.35) * mm, "radius": 1.38 * mm});
            skCircle(sketch, "E39", {"center": v(-39.75, 28.35) * mm, "radius": 1.38 * mm});
            skCircle(sketch, "E40", {"center": v(-2.02, 28.35) * mm, "radius": 1.38 * mm});
            skSolve(sketch);
        }
        {
            var Q0;
            Q0 = qSketchRegion(id + "F44", true);
            extrude(context, id + "F45", {"entities" : qUnion([Q0]), "operationType" : NewBodyOperationType.ADD, "depth" : 15 * mm});
        }
        {
            var Q0;
            {var subQ0=sQuery(id+"F8.wireOp",EDGE,"E4.sketch_text.stroke-18");var subQ1=sQuery(id+"F8.wireOp",EDGE,"E4.sketch_text.stroke-17");var subQ2=sQuery(id+"F0.wireOp",EDGE,"E0.bottom");var subQ3=sQuery(id+"F8.wireOp",EDGE,"E4.sketch_text.stroke-14");var subQ4=sQuery(id+"F8.wireOp",EDGE,"E4.sketch_text.stroke-13");var subQ5=sQuery(id+"F8.wireOp",EDGE,"E4.sketch_text.stroke-12");var subQ6=sQuery(id+"F8.wireOp",EDGE,"E4.sketch_text.stroke-11");var subQ7=sQuery(id+"F8.wireOp",EDGE,"E4.sketch_text.stroke-10");var subQ8=sQuery(id+"F8.wireOp",EDGE,"E4.sketch_text.stroke-9");var subQ9=sQuery(id+"F8.wireOp",EDGE,"E4.sketch_text.stroke-8");var subQ10=sQuery(id+"F4.wireOp",EDGE,"E2.right");var subQ11=sQuery(id+"F4.wireOp",EDGE,"E2.left");var subQ12=sQuery(id+"F4.wireOp",EDGE,"E2.top");var subQ13=sQuery(id+"F4.wireOp",EDGE,"E2.bottom");var subQ14=makeQuery(id+"F5.opExtrude","CAP_FACE",FACE,{"disambiguationData":[OSD([subQ13,subQ12,subQ11,subQ10])],"isStart":false});var subQ18=sQuery(id+"F8.wireOp",EDGE,"E4.sketch_text.stroke-6");var subQ19=sQuery(id+"F8.wireOp",EDGE,"E4.sketch_text.stroke-1");var subQ20=sQuery(id+"F2.wireOp",EDGE,"E1.sketch_text.stroke-9");var subQ22=sQuery(id+"F6.wireOp",EDGE,"E3.sketch_text.stroke-1");var subQ23=sQuery(id+"F2.wireOp",EDGE,"E1.sketch_text.stroke-7");var subQ25=sQuery(id+"F20.wireOp",EDGE,"E10.right");var subQ26=sQuery(id+"F8.wireOp",EDGE,"E4.sketch_text.stroke-16");var subQ27=sQuery(id+"F2.wireOp",EDGE,"E1.sketch_text.stroke-5");var subQ29=sQuery(id+"F20.wireOp",EDGE,"E10.top");var subQ30=sQuery(id+"F2.wireOp",EDGE,"E1.sketch_text.stroke-3");var subQ31=sQuery(id+"F2.wireOp",EDGE,"E1.sketch_text.stroke-8");var subQ32=sQuery(id+"F6.wireOp",EDGE,"E3.sketch_text.stroke-9");var subQ33=sQuery(id+"F2.wireOp",EDGE,"E1.sketch_text.stroke-1");var subQ34=sQuery(id+"F6.wireOp",EDGE,"E3.sketch_text.stroke-13");var subQ35=sQuery(id+"F6.wireOp",EDGE,"E3.sketch_text.stroke-12");var subQ36=sQuery(id+"F6.wireOp",EDGE,"E3.sketch_text.stroke-11");var subQ37=sQuery(id+"F6.wireOp",EDGE,"E3.sketch_text.stroke-10");var subQ38=sQuery(id+"F6.wireOp",EDGE,"E3.sketch_text.stroke-8");var subQ39=sQuery(id+"F6.wireOp",EDGE,"E3.sketch_text.stroke-7");var subQ40=sQuery(id+"F6.wireOp",EDGE,"E3.sketch_text.stroke-6");var subQ41=sQuery(id+"F6.wireOp",EDGE,"E3.sketch_text.stroke-5");var subQ42=sQuery(id+"F6.wireOp",EDGE,"E3.sketch_text.stroke-4");var subQ43=sQuery(id+"F6.wireOp",EDGE,"E3.sketch_text.stroke-3");var subQ44=sQuery(id+"F6.wireOp",EDGE,"E3.sketch_text.stroke-2");var subQ45=sQuery(id+"F6.wireOp",EDGE,"E3.sketch_text.stroke-0");var subQ47=sQuery(id+"F10.wireOp",EDGE,"E5.right");var subQ48=sQuery(id+"F10.wireOp",EDGE,"E5.left");var subQ49=sQuery(id+"F10.wireOp",EDGE,"E5.top");var subQ50=sQuery(id+"F10.wireOp",EDGE,"E5.bottom");var subQ51=makeQuery(id+"F11.opExtrude","CAP_FACE",FACE,{"disambiguationData":[OSD([subQ50,subQ49,subQ48,subQ47])],"isStart":false});var subQ52=sQuery(id+"F0.wireOp",EDGE,"E0.right");var subQ53=sQuery(id+"F0.wireOp",EDGE,"E0.left");var subQ54=sQuery(id+"F0.wireOp",EDGE,"E0.top");var subQ55=makeQuery(id+"F1.opExtrude","CAP_FACE",FACE,{"disambiguationData":[OSD([subQ2,subQ54,subQ53,subQ52])],"isStart":false});var subQ57=makeQuery(id+"F7.opExtrude","CAP_FACE",FACE,{"disambiguationData":[OSD([subQ45,subQ22,subQ44,subQ43,subQ42,subQ41,subQ40,subQ39,subQ38,subQ32,subQ37,subQ36,subQ35,subQ34])],"isStart":false});var subQ60=sQuery(id+"F8.wireOp",EDGE,"E4.sketch_text.stroke-15");var subQ61=sQuery(id+"F8.wireOp",EDGE,"E4.sketch_text.stroke-7");var subQ62=sQuery(id+"F8.wireOp",EDGE,"E4.sketch_text.stroke-5");var subQ63=sQuery(id+"F8.wireOp",EDGE,"E4.sketch_text.stroke-4");var subQ64=sQuery(id+"F8.wireOp",EDGE,"E4.sketch_text.stroke-3");var subQ65=sQuery(id+"F8.wireOp",EDGE,"E4.sketch_text.stroke-2");var subQ66=sQuery(id+"F8.wireOp",EDGE,"E4.sketch_text.stroke-0");var subQ68=makeQuery(id+"F9.opExtrude","CAP_FACE",FACE,{"disambiguationData":[OSD([subQ66,subQ19,subQ65,subQ64,subQ63,subQ62,subQ18,subQ61,subQ9,subQ8,subQ7,subQ6,subQ5,subQ4,subQ3,subQ60,subQ26,subQ1,subQ0])],"isStart":false});var subQ71=sQuery(id+"F2.wireOp",EDGE,"E1.sketch_text.stroke-2");var subQ72=sQuery(id+"F2.wireOp",EDGE,"E1.sketch_text.stroke-12");var subQ73=sQuery(id+"F2.wireOp",EDGE,"E1.sketch_text.stroke-11");var subQ75=sQuery(id+"F2.wireOp",EDGE,"E1.sketch_text.stroke-10");var subQ76=sQuery(id+"F2.wireOp",EDGE,"E1.sketch_text.stroke-6");var subQ77=sQuery(id+"F2.wireOp",EDGE,"E1.sketch_text.stroke-4");var subQ78=sQuery(id+"F2.wireOp",EDGE,"E1.sketch_text.stroke-0");var subQ80=makeQuery(id+"F3.opExtrude","CAP_FACE",FACE,{"disambiguationData":[OSD([subQ78,subQ33,subQ71,subQ30,subQ77,subQ27,subQ76,subQ23,subQ31,subQ20,subQ75,subQ73,subQ72])],"isStart":false});var subQ82=sQuery(id+"F20.wireOp",EDGE,"E10.left");Q0=makeQuery(id+"F45.boolean.opBoolean","MERGE",FACE,{"derivedFrom":[makeQuery(id+"F43.boolean.opBoolean","MERGE",FACE,{"derivedFrom":[makeQuery(id+"F25.boolean.opBoolean","MERGE",FACE,{"derivedFrom":[makeQuery(id+"F19.opExtrude","CAP_FACE",FACE,{"disambiguationData":[OSD([sQuery(id+"F18.wireOp",EDGE,"E9.bottom"),sQuery(id+"F18.wireOp",EDGE,"E9.top"),sQuery(id+"F18.wireOp",EDGE,"E9.left"),sQuery(id+"F18.wireOp",EDGE,"E9.right")])],"isStart":false}),makeQuery(id+"FRnRs9VXwVQGoIw_4.boolean.opBoolean","SPLIT",FACE,{"disambiguationData":[TD([makeQuery(id+"F1.opExtrude","SWEPT_FACE",FACE,{"disambiguationData":[OSD([subQ2])]})])],"derivedFrom":makeQuery(id+"F21.boolean.opBoolean","MERGE",FACE,{"derivedFrom":[subQ80,subQ14,makeQuery(id+"F11.boolean.opBoolean","MERGE",FACE,{"derivedFrom":[makeQuery(id+"F9.boolean.opBoolean","MERGE",FACE,{"derivedFrom":[makeQuery(id+"F7.boolean.opBoolean","MERGE",FACE,{"derivedFrom":[subQ55,subQ57]}),subQ68]}),subQ51]}),makeQuery(id+"F21.opExtrude","CAP_FACE",FACE,{"disambiguationData":[OSD([sQuery(id+"F20.wireOp",EDGE,"E10.bottom"),subQ29,subQ82,subQ25])],"isStart":false})]})})]}),makeQuery(id+"F43.opExtrude","CAP_FACE",FACE,{"disambiguationData":[OSD([sQuery(id+"F42.wireOp",EDGE,"E29"),sQuery(id+"F42.wireOp",EDGE,"E30"),sQuery(id+"F42.wireOp",EDGE,"E32"),sQuery(id+"F42.wireOp",EDGE,"E33"),sQuery(id+"F42.wireOp",EDGE,"E34"),sQuery(id+"F42.wireOp",EDGE,"E35"),sQuery(id+"F42.wireOp",EDGE,"E36")])],"isStart":false})]}),makeQuery(id+"F45.opExtrude","CAP_FACE",FACE,{"disambiguationData":[OSD([sQuery(id+"F44.wireOp",EDGE,"E38")])],"isStart":false}),makeQuery(id+"F45.opExtrude","CAP_FACE",FACE,{"disambiguationData":[OSD([sQuery(id+"F44.wireOp",EDGE,"E39")])],"isStart":false}),makeQuery(id+"F45.opExtrude","CAP_FACE",FACE,{"disambiguationData":[OSD([sQuery(id+"F44.wireOp",EDGE,"E40")])],"isStart":false})]});}
            var sketch = newSketch(context, id + "F46", { "sketchPlane" : qUnion([Q0])});
            skSolve(sketch);
        }
        {
            var Q0;
            {var subQ24=sQuery(id+"F2.wireOp",EDGE,"E1.sketch_text.stroke-1");Q0=makeQuery(id+"F46.imprint","IMPRINT",FACE,{"disambiguationData":[TD([[makeQuery(id+"F46.imprint","IMPRINT",EDGE,{"derivedFrom":makeQuery(id+"F3.opExtrude","CAP_EDGE",EDGE,{"disambiguationData":[OSD([subQ24])],"isStart":false})}),-1.0]])]});}
            var sketch = newSketch(context, id + "F47", { "sketchPlane" : qUnion([Q0])});
            skText(sketch, "E41", { "text": "#7", "fontName": "OpenSans-Bold.ttf"});
            const initialGuessF47  = {"E41": [-0.0057, -0.0192, 1, 0, 0.0078]};
            skSetInitialGuess(sketch, initialGuessF47);
            skSolve(sketch);
        }
        {
            var Q0;
            Q0 = qSketchRegion(id + "F47", true);
            extrude(context, id + "F48", {"entities" : qUnion([Q0]), "operationType" : NewBodyOperationType.REMOVE, "oppositeDirection" : true, "depth" : 5 * mm});
        }
    });
